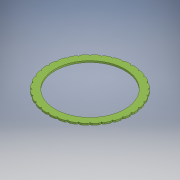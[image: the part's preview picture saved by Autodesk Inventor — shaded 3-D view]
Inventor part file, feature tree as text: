
AUTODESK INVENTOR PART (.ipt)
format: ipt  version: 2020 (Build 240168000, 168)  size: 325,120 bytes
history: native  units: mm
features: other x2, sketch x2, extrude x1
ambient origin geometry x8: Origin, YZ Plane, XZ Plane, XY Plane, X Axis, Y Axis, Z Axis, Center Point
bodies: Body1 (feature_tree)
feature tree (5):
  other  "tsop_lid"
  other  "Твердое тело1"
  extrude  "Выдавливание1"  Depth=10.0mm
  sketch  "Эскиз1"
  sketch  "Эскиз3"
